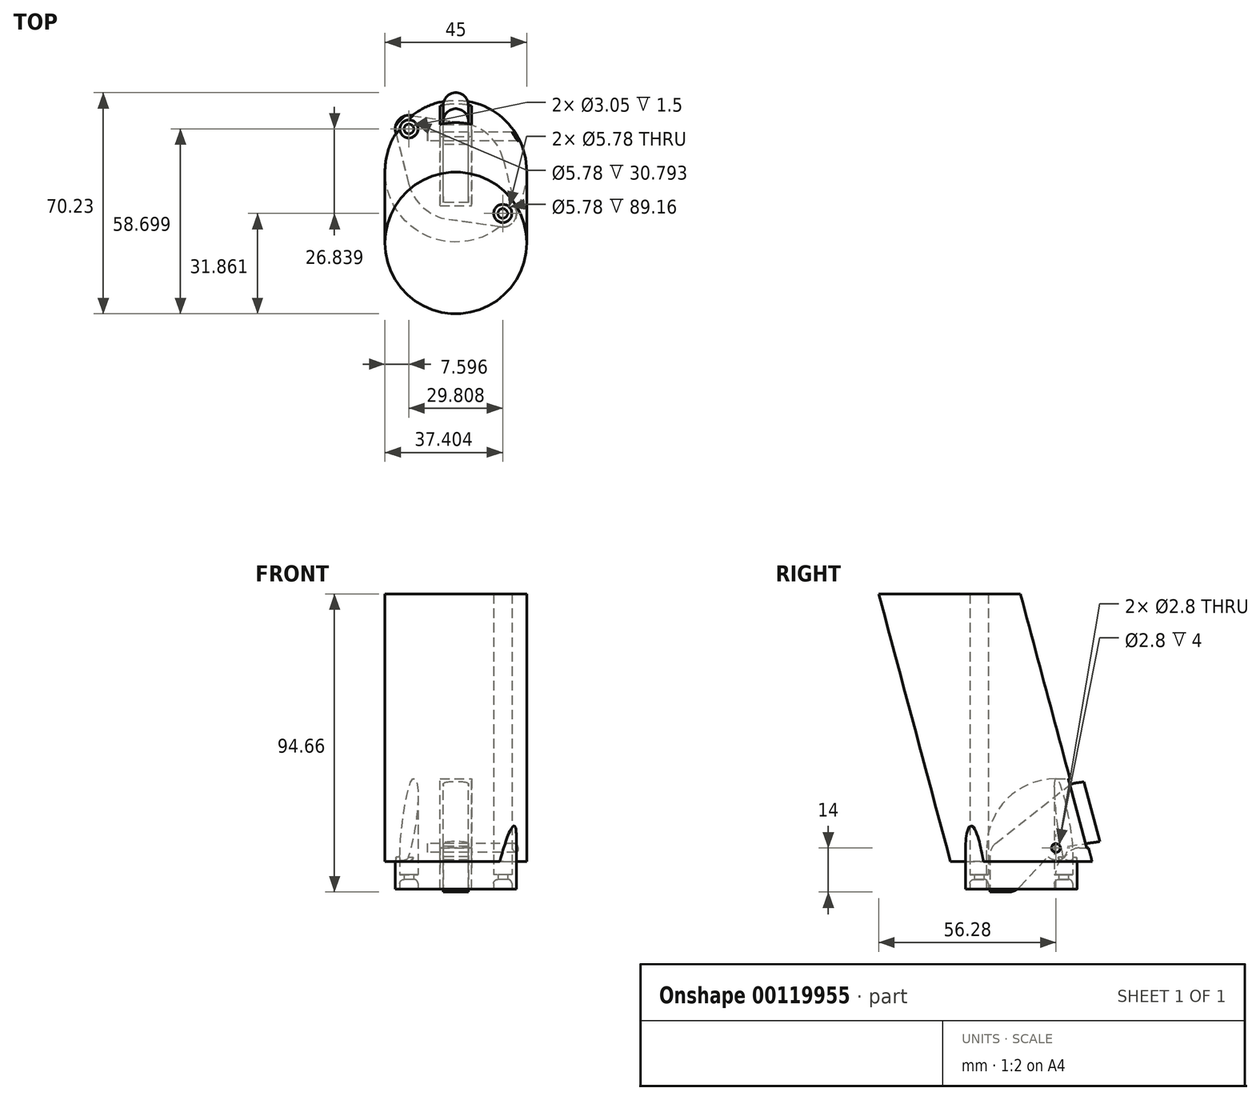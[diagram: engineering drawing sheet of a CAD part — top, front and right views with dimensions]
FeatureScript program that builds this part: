
annotation { "Feature Type Name" : "Feature", "Feature Type Description" : "" }
export const myFeature = defineFeature(function(context is Context, id is Id, definition is map)
    precondition{}
    {
        {
            var Q0;
            Q0=qCreatedBy(makeId("Top.planeOp"),FACE);
            var sketch = newSketch(context, id + "F0", { "sketchPlane" : qUnion([Q0])});
            skLineSegment(sketch, "E0", {"start": v(0, 52.12) * mm, "end": v(0, -55.22) * mm, "construction": true});
            skCircle(sketch, "E1", {"center": v(0, 0) * mm, "radius": 15.5 * mm});
            skCircle(sketch, "E2", {"center": v(-14.9, 13.42) * mm, "radius": 2.9 * mm});
            skCircle(sketch, "E3", {"center": v(-14.9, 13.42) * mm, "radius": 4.34 * mm});
            skCircle(sketch, "E4", {"center": v(-14.9, 13.42) * mm, "radius": 1.52 * mm});
            skCircle(sketch, "E5", {"center": v(14.9, -13.42) * mm, "radius": 1.52 * mm});
            skCircle(sketch, "E6", {"center": v(14.9, -13.42) * mm, "radius": 2.9 * mm});
            skCircle(sketch, "E7", {"center": v(14.9, -13.42) * mm, "radius": 4.34 * mm});
            skLineSegment(sketch, "E8", {"start": v(0, 0) * mm, "end": v(-14.9, 13.42) * mm, "construction": true});
            skLineSegment(sketch, "E9", {"start": v(0, 0) * mm, "end": v(14.9, -13.42) * mm, "construction": true});
            skLineSegment(sketch, "E10", {"start": v(-14.28, 17.72) * mm, "end": v(2.21, 15.34) * mm});
            skLineSegment(sketch, "E11", {"start": v(-19.12, 12.35) * mm, "end": v(-15.03, -3.8) * mm});
            skLineSegment(sketch, "E12", {"start": v(14.28, -17.72) * mm, "end": v(-2.21, -15.34) * mm});
            skLineSegment(sketch, "E13", {"start": v(15.03, 3.8) * mm, "end": v(19.12, -12.35) * mm});
            skSolve(sketch);
        }
        {
            var Q0;
            Q0=makeQuery(id+"F0.imprint","IMPRINT",FACE,{"disambiguationData":[TD([[makeQuery(id+"F0.imprint","IMPRINT",EDGE,{"derivedFrom":sQuery(id+"F0.wireOp",EDGE,"E2")}),-1.0]])]});
            var Q1;
            {var subQ0=sQuery(id+"F0.wireOp",EDGE,"E10");Q1=makeQuery(id+"F0.imprint","IMPRINT",FACE,{"disambiguationData":[TD([[makeQuery(id+"F0.imprint","IMPRINT",EDGE,{"derivedFrom":subQ0}),-1.0]])]});}
            var Q2;
            {var subQ0=sQuery(id+"F0.wireOp",EDGE,"E1");var subQ1=makeQuery(id+"F0.imprint","INTERSECT",VERTEX,{"derivedFrom":[subQ0,sQuery(id+"F0.wireOp",EDGE,"E10")]});Q2=makeQuery(id+"F0.imprint","IMPRINT",FACE,{"disambiguationData":[TD([[makeQuery(id+"F0.imprint","IMPRINT",EDGE,{"disambiguationData":[TD([[subQ1,1.0]])],"derivedFrom":subQ0}),1.0]])]});}
            var Q3;
            {var subQ0=sQuery(id+"F0.wireOp",EDGE,"E12");Q3=makeQuery(id+"F0.imprint","IMPRINT",FACE,{"disambiguationData":[TD([[makeQuery(id+"F0.imprint","IMPRINT",EDGE,{"derivedFrom":subQ0}),-1.0]])]});}
            var Q4;
            Q4=makeQuery(id+"F0.imprint","IMPRINT",FACE,{"disambiguationData":[TD([[makeQuery(id+"F0.imprint","IMPRINT",EDGE,{"derivedFrom":sQuery(id+"F0.wireOp",EDGE,"E6")}),-1.0]])]});
            extrude(context, id + "F1", {"entities" : qUnion([Q0, Q1, Q2, Q3, Q4]), "depth" : 8.66 * mm});
        }
        {
            var Q0;
            Q0=makeQuery(id+"F0.imprint","IMPRINT",FACE,{"disambiguationData":[TD([[makeQuery(id+"F0.imprint","IMPRINT",EDGE,{"derivedFrom":sQuery(id+"F0.wireOp",EDGE,"E5")}),-1.0]])]});
            var Q1;
            Q1=makeQuery(id+"F0.imprint","IMPRINT",FACE,{"disambiguationData":[TD([[makeQuery(id+"F0.imprint","IMPRINT",EDGE,{"derivedFrom":sQuery(id+"F0.wireOp",EDGE,"E2")}),1.0]])]});
            extrude(context, id + "F2", {"entities" : qUnion([Q0, Q1]), "operationType" : NewBodyOperationType.ADD, "depth" : 4.5 * mm});
        }
        {
            var Q0;
            Q0=makeQuery(id+"F0.imprint","IMPRINT",FACE,{"disambiguationData":[TD([[makeQuery(id+"F0.imprint","IMPRINT",EDGE,{"derivedFrom":sQuery(id+"F0.wireOp",EDGE,"E5")}),-1.0]])]});
            var Q1;
            Q1=makeQuery(id+"F0.imprint","IMPRINT",FACE,{"disambiguationData":[TD([[makeQuery(id+"F0.imprint","IMPRINT",EDGE,{"derivedFrom":sQuery(id+"F0.wireOp",EDGE,"E2")}),1.0]])]});
            extrude(context, id + "F3", {"entities" : qUnion([Q0, Q1]), "operationType" : NewBodyOperationType.REMOVE, "depth" : 3 * mm});
        }
        {
            var Q0;
            Q0=makeQuery(id+"F3.boolean.opBoolean","COPY",EDGE,{"derivedFrom":makeQuery(id+"F3.opExtrude","CAP_EDGE",EDGE,{"disambiguationData":[OSD([sQuery(id+"F0.wireOp",EDGE,"E6")])],"isStart":false})});
            var Q1;
            Q1=makeQuery(id+"F3.boolean.opBoolean","COPY",EDGE,{"derivedFrom":makeQuery(id+"F3.opExtrude","CAP_EDGE",EDGE,{"disambiguationData":[OSD([sQuery(id+"F0.wireOp",EDGE,"E2")])],"isStart":false})});
            fillet(context, id + "F4", {"entities" : qUnion([Q0, Q1]), "radius" : 1.3 * mm, "tangentPropagation" : true, "allowEdgeOverflow" : false});
        }
        {
            var Q0;
            Q0=makeQuery(id+"F1.opExtrude","CAP_FACE",FACE,{"disambiguationData":[OSD([sQuery(id+"F0.wireOp",EDGE,"E1"),sQuery(id+"F0.wireOp",EDGE,"E2"),sQuery(id+"F0.wireOp",EDGE,"E3"),sQuery(id+"F0.wireOp",EDGE,"E6"),sQuery(id+"F0.wireOp",EDGE,"E7"),sQuery(id+"F0.wireOp",EDGE,"E10"),sQuery(id+"F0.wireOp",EDGE,"E11"),sQuery(id+"F0.wireOp",EDGE,"E12"),sQuery(id+"F0.wireOp",EDGE,"E13")])],"isStart":false});
            var sketch = newSketch(context, id + "F5", { "sketchPlane" : qUnion([Q0])});
            skCircle(sketch, "E14", {"center": v(0, 0) * mm, "radius": 22.5 * mm});
            skSolve(sketch);
        }
        {
            var Q0;
            Q0=qCreatedBy(makeId("Right.planeOp"),FACE);
            var sketch = newSketch(context, id + "F6", { "sketchPlane" : qUnion([Q0])});
            skLineSegment(sketch, "E15", {"start": v(0, 8.66) * mm, "end": v(-22.78, 93.66) * mm});
            skLineSegment(sketch, "E16.0", {"start": v(3.8, 8.66) * mm, "end": v(-12.35, 8.66) * mm});
            skSolve(sketch);
        }
        {
            var Q0;
            {var subQ3=sQuery(id+"F0.wireOp",EDGE,"E1");var subQ14=sQuery(id+"F0.wireOp",EDGE,"E10");var subQ15=makeQuery(id+"F1.opExtrude","CAP_EDGE",EDGE,{"disambiguationData":[OSD([subQ3]),TDD([makeQuery(id+"F0.imprint","IMPRINT",EDGE,{"disambiguationData":[TD([[makeQuery(id+"F0.imprint","INTERSECT",VERTEX,{"derivedFrom":[subQ3,subQ14]}),1.0]])],"derivedFrom":subQ3})])],"isStart":false});Q0=makeQuery(id+"F5.imprint","IMPRINT",FACE,{"disambiguationData":[TD([[makeQuery(id+"F5.imprint","IMPRINT",EDGE,{"derivedFrom":subQ15}),1.0]])]});}
            var Q1;
            {var subQ0=sQuery(id+"F5.wireOp",EDGE,"E14");var subQ1=makeQuery(id+"F1.opExtrude","CAP_EDGE",EDGE,{"disambiguationData":[OSD([sQuery(id+"F0.wireOp",EDGE,"E6")])],"isStart":false});var subQ2=makeQuery(id+"F5.imprint","INTERSECT",VERTEX,{"disambiguationData":[OD(0.0)],"derivedFrom":[subQ1,subQ0]});Q1=makeQuery(id+"F5.imprint","IMPRINT",FACE,{"disambiguationData":[TD([[makeQuery(id+"F5.imprint","IMPRINT",EDGE,{"disambiguationData":[TD([[subQ2,-1.0]])],"derivedFrom":subQ0}),1.0]])]});}
            var Q2;
            {var subQ0=sQuery(id+"F5.wireOp",EDGE,"E14");var subQ1=makeQuery(id+"F1.opExtrude","CAP_EDGE",EDGE,{"disambiguationData":[OSD([sQuery(id+"F0.wireOp",EDGE,"E2")])],"isStart":false});var subQ2=makeQuery(id+"F5.imprint","INTERSECT",VERTEX,{"disambiguationData":[OD(0.0)],"derivedFrom":[subQ1,subQ0]});Q2=makeQuery(id+"F5.imprint","IMPRINT",FACE,{"disambiguationData":[TD([[makeQuery(id+"F5.imprint","IMPRINT",EDGE,{"disambiguationData":[TD([[subQ2,-1.0]])],"derivedFrom":subQ0}),1.0]])]});}
            var Q3;
            {var subQ1=sQuery(id+"F0.wireOp",EDGE,"E10");var subQ7=sQuery(id+"F0.wireOp",EDGE,"E1");var subQ8=makeQuery(id+"F1.opExtrude","CAP_EDGE",EDGE,{"disambiguationData":[OSD([subQ7]),TDD([makeQuery(id+"F0.imprint","IMPRINT",EDGE,{"disambiguationData":[TD([[makeQuery(id+"F0.imprint","INTERSECT",VERTEX,{"derivedFrom":[subQ7,subQ1]}),1.0]])],"derivedFrom":subQ7})])],"isStart":false});Q3=makeQuery(id+"F5.imprint","IMPRINT",FACE,{"disambiguationData":[TD([[makeQuery(id+"F5.imprint","IMPRINT",EDGE,{"derivedFrom":subQ8}),-1.0]])]});}
            var Q4;
            {var subQ1=sQuery(id+"F0.wireOp",EDGE,"E11");var subQ7=sQuery(id+"F0.wireOp",EDGE,"E1");var subQ8=makeQuery(id+"F1.opExtrude","CAP_EDGE",EDGE,{"disambiguationData":[OSD([subQ7]),TDD([makeQuery(id+"F0.imprint","IMPRINT",EDGE,{"disambiguationData":[TD([[makeQuery(id+"F0.imprint","INTERSECT",VERTEX,{"derivedFrom":[subQ7,subQ1]}),-1.0]])],"derivedFrom":subQ7})])],"isStart":false});Q4=makeQuery(id+"F5.imprint","IMPRINT",FACE,{"disambiguationData":[TD([[makeQuery(id+"F5.imprint","IMPRINT",EDGE,{"derivedFrom":subQ8}),-1.0]])]});}
            var Q5;
            Q5=sQuery(id+"F6.wireOp",EDGE,"E15");
            sweep(context, id + "F7", {"operationType" : NewBodyOperationType.ADD, "profiles" : qUnion([Q0, Q1, Q2, Q3, Q4]), "path" : qUnion([Q5])});
        }
        {
            var Q0;
            {var subQ0=sQuery(id+"F0.wireOp",EDGE,"E13");var subQ1=sQuery(id+"F0.wireOp",EDGE,"E12");var subQ2=sQuery(id+"F0.wireOp",EDGE,"E7");var subQ4=sQuery(id+"F0.wireOp",EDGE,"E6");Q0=makeQuery(id+"F7.boolean.opBoolean","SPLIT",FACE,{"disambiguationData":[TD([makeQuery(id+"F1.opExtrude","SWEPT_FACE",FACE,{"disambiguationData":[OSD([subQ4])]})])],"derivedFrom":makeQuery(id+"F1.opExtrude","CAP_FACE",FACE,{"disambiguationData":[OSD([sQuery(id+"F0.wireOp",EDGE,"E1"),sQuery(id+"F0.wireOp",EDGE,"E2"),sQuery(id+"F0.wireOp",EDGE,"E3"),subQ4,subQ2,sQuery(id+"F0.wireOp",EDGE,"E10"),sQuery(id+"F0.wireOp",EDGE,"E11"),subQ1,subQ0])],"isStart":false})});}
            var sketch = newSketch(context, id + "F8", { "sketchPlane" : qUnion([Q0])});
            skArc(sketch, "E17.0", {"start": v(15.59, -16.23) * mm, "mid": v(17.05, -15.35) * mm, "end": v(17.77, -13.8) * mm});
            skArc(sketch, "E18.0", {"start": v(17.77, -13.8) * mm, "mid": v(12.76, -11.49) * mm, "end": v(15.59, -16.23) * mm});
            skSolve(sketch);
        }
        {
            var Q0;
            {var subQ0=sQuery(id+"F0.wireOp",EDGE,"E6");var subQ1=sQuery(id+"F5.wireOp",EDGE,"E14");Q0=makeQuery(id+"F7.boolean.opBoolean","SPLIT",FACE,{"disambiguationData":[TD([makeQuery(id+"F1.opExtrude","SWEPT_FACE",FACE,{"disambiguationData":[OSD([subQ0])]})])],"derivedFrom":makeQuery(id+"F7.opSweep","CAP_FACE",FACE,{"disambiguationData":[OSD([subQ1,sQuery(id+"F6.wireOp",VERTEX,"E15.start")])],"isStart":true})});}
            var Q1;
            {var subQ0=sQuery(id+"F0.wireOp",EDGE,"E2");var subQ1=sQuery(id+"F5.wireOp",EDGE,"E14");Q1=makeQuery(id+"F7.boolean.opBoolean","SPLIT",FACE,{"disambiguationData":[TD([makeQuery(id+"F1.opExtrude","SWEPT_FACE",FACE,{"disambiguationData":[OSD([subQ0])]})])],"derivedFrom":makeQuery(id+"F7.opSweep","CAP_FACE",FACE,{"disambiguationData":[OSD([subQ1,sQuery(id+"F6.wireOp",VERTEX,"E15.start")])],"isStart":true})});}
            var Q2;
            Q2=makeQuery(id+"F8.imprint","IMPRINT",FACE,{"disambiguationData":[TD([[makeQuery(id+"F8.imprint","IMPRINT",EDGE,{"derivedFrom":sQuery(id+"F8.wireOp",EDGE,"E17.0")}),1.0]])]});
            extrude(context, id + "F9", {"entities" : qUnion([Q0, Q1, Q2]), "operationType" : NewBodyOperationType.REMOVE, "endBound" : BoundingType.THROUGH_ALL, "oppositeDirection" : true, "depth" : 25 * mm});
        }
        {
            var Q0;
            {var subQ0=sQuery(id+"F6.wireOp",VERTEX,"E15.start");var subQ1=sQuery(id+"F5.wireOp",EDGE,"E14");var subQ2=sQuery(id+"F0.wireOp",EDGE,"E2");var subQ3=sQuery(id+"F0.wireOp",EDGE,"E10");Q0=makeQuery(id+"F7.boolean.opBoolean","SPLIT",EDGE,{"disambiguationData":[TD([makeQuery(id+"F1.opExtrude","CAP_FACE",FACE,{"disambiguationData":[OSD([sQuery(id+"F0.wireOp",EDGE,"E1"),subQ2,sQuery(id+"F0.wireOp",EDGE,"E3"),sQuery(id+"F0.wireOp",EDGE,"E6"),sQuery(id+"F0.wireOp",EDGE,"E7"),subQ3,sQuery(id+"F0.wireOp",EDGE,"E11"),sQuery(id+"F0.wireOp",EDGE,"E12"),sQuery(id+"F0.wireOp",EDGE,"E13")])],"isStart":false}),makeQuery(id+"F1.opExtrude","SWEPT_FACE",FACE,{"disambiguationData":[OSD([subQ2])]}),makeQuery(id+"F1.opExtrude","SWEPT_FACE",FACE,{"disambiguationData":[OSD([subQ3])]}),makeQuery(id+"F7.opSweep","CAP_FACE",FACE,{"disambiguationData":[OSD([subQ1,subQ0])],"isStart":true}),makeQuery(id+"F7.opSweep","SWEPT_FACE",FACE,{"disambiguationData":[OSD([subQ1,sQuery(id+"F6.wireOp",EDGE,"E15")])]})])],"derivedFrom":makeQuery(id+"F7.opSweep","CAP_EDGE",EDGE,{"disambiguationData":[OSD([subQ1,subQ0])],"isStart":true})});}
            var Q1;
            {var subQ0=sQuery(id+"F6.wireOp",VERTEX,"E15.start");var subQ1=sQuery(id+"F5.wireOp",EDGE,"E14");var subQ2=sQuery(id+"F0.wireOp",EDGE,"E11");var subQ3=sQuery(id+"F0.wireOp",EDGE,"E2");Q1=makeQuery(id+"F7.boolean.opBoolean","SPLIT",EDGE,{"disambiguationData":[TD([makeQuery(id+"F1.opExtrude","CAP_FACE",FACE,{"disambiguationData":[OSD([sQuery(id+"F0.wireOp",EDGE,"E1"),subQ3,sQuery(id+"F0.wireOp",EDGE,"E3"),sQuery(id+"F0.wireOp",EDGE,"E6"),sQuery(id+"F0.wireOp",EDGE,"E7"),sQuery(id+"F0.wireOp",EDGE,"E10"),subQ2,sQuery(id+"F0.wireOp",EDGE,"E12"),sQuery(id+"F0.wireOp",EDGE,"E13")])],"isStart":false}),makeQuery(id+"F1.opExtrude","SWEPT_FACE",FACE,{"disambiguationData":[OSD([subQ3])]}),makeQuery(id+"F1.opExtrude","SWEPT_FACE",FACE,{"disambiguationData":[OSD([subQ2])]}),makeQuery(id+"F7.opSweep","CAP_FACE",FACE,{"disambiguationData":[OSD([subQ1,subQ0])],"isStart":true}),makeQuery(id+"F7.opSweep","SWEPT_FACE",FACE,{"disambiguationData":[OSD([subQ1,sQuery(id+"F6.wireOp",EDGE,"E15")])]})])],"derivedFrom":makeQuery(id+"F7.opSweep","CAP_EDGE",EDGE,{"disambiguationData":[OSD([subQ1,subQ0])],"isStart":true})});}
            fillet(context, id + "F10", {"entities" : qUnion([Q0, Q1]), "radius" : 1.7 * mm, "tangentPropagation" : true, "allowEdgeOverflow" : false});
        }
        {
            var Q0;
            {var subQ0=sQuery(id+"F0.wireOp",EDGE,"E13");var subQ1=sQuery(id+"F0.wireOp",EDGE,"E12");var subQ2=sQuery(id+"F0.wireOp",EDGE,"E7");var subQ4=sQuery(id+"F0.wireOp",EDGE,"E6");Q0=makeQuery(id+"F7.boolean.opBoolean","SPLIT",FACE,{"disambiguationData":[TD([makeQuery(id+"F1.opExtrude","SWEPT_FACE",FACE,{"disambiguationData":[OSD([subQ4])]})])],"derivedFrom":makeQuery(id+"F1.opExtrude","CAP_FACE",FACE,{"disambiguationData":[OSD([sQuery(id+"F0.wireOp",EDGE,"E1"),sQuery(id+"F0.wireOp",EDGE,"E2"),sQuery(id+"F0.wireOp",EDGE,"E3"),subQ4,subQ2,sQuery(id+"F0.wireOp",EDGE,"E10"),sQuery(id+"F0.wireOp",EDGE,"E11"),subQ1,subQ0])],"isStart":false})});}
            var Q1;
            Q1=makeQuery(id+"F1.opExtrude","SWEPT_BODY",BODY,{"disambiguationData":[OSD([sQuery(id+"F0.wireOp",EDGE,"E1"),sQuery(id+"F0.wireOp",EDGE,"E2"),sQuery(id+"F0.wireOp",EDGE,"E3"),sQuery(id+"F0.wireOp",EDGE,"E6"),sQuery(id+"F0.wireOp",EDGE,"E7"),sQuery(id+"F0.wireOp",EDGE,"E10"),sQuery(id+"F0.wireOp",EDGE,"E11"),sQuery(id+"F0.wireOp",EDGE,"E12"),sQuery(id+"F0.wireOp",EDGE,"E13")])]});
            extrude(context, id + "F11", {"entities" : qUnion([Q0]), "operationType" : NewBodyOperationType.ADD, "endBound" : BoundingType.UP_TO_BODY, "endBoundEntityBody" : qUnion([Q1]), "depth" : 25 * mm});
        }
        {
            var Q0;
            Q0=qCreatedBy(makeId("Right.planeOp"),FACE);
            var sketch = newSketch(context, id + "F12", { "sketchPlane" : qUnion([Q0])});
            skLineSegment(sketch, "E19", {"start": v(-11, 0) * mm, "end": v(11, 0) * mm});
            skLineSegment(sketch, "E20", {"start": v(-11, 0) * mm, "end": v(-11, 13) * mm});
            skLineSegment(sketch, "E21", {"start": v(11, 0) * mm, "end": v(11, 13) * mm});
            skArc(sketch, "E22", {"start": v(-11, 13) * mm, "mid": v(-4.56, 28.56) * mm, "end": v(11, 35) * mm});
            skLineSegment(sketch, "E23", {"start": v(11, 35) * mm, "end": v(17.1, 35) * mm});
            skLineSegment(sketch, "E24", {"start": v(11, 13) * mm, "end": v(23, 13) * mm});
            skLineSegment(sketch, "E25", {"start": v(23, 13) * mm, "end": v(17.1, 35) * mm});
            skCircle(sketch, "E26", {"center": v(11, 13) * mm, "radius": 1.4 * mm});
            skCircle(sketch, "E27", {"center": v(11, 13) * mm, "radius": 4 * mm});
            skCircle(sketch, "E28", {"center": v(11, 13) * mm, "radius": 3.75 * mm});
            skLineSegment(sketch, "E29", {"start": v(-10, 13) * mm, "end": v(-10, -1) * mm});
            skLineSegment(sketch, "E30", {"start": v(-10, -1) * mm, "end": v(-2, -1) * mm});
            skLineSegment(sketch, "E31", {"start": v(-2, -1) * mm, "end": v(11, 13) * mm});
            skLineSegment(sketch, "E32", {"start": v(11, 13) * mm, "end": v(24.95, 15.03) * mm});
            skLineSegment(sketch, "E33", {"start": v(24.95, 15.03) * mm, "end": v(19.86, 34.02) * mm});
            skLineSegment(sketch, "E34", {"start": v(15.9, 33.44) * mm, "end": v(19.86, 34.02) * mm});
            skLineSegment(sketch, "E35", {"start": v(-10, 13) * mm, "end": v(15.9, 33.44) * mm});
            skSolve(sketch);
        }
        {
            var Q0;
            {var subQ1=sQuery(id+"F12.wireOp",EDGE,"E20");Q0=makeQuery(id+"F12.imprint","IMPRINT",FACE,{"disambiguationData":[TD([[makeQuery(id+"F12.imprint","IMPRINT",EDGE,{"derivedFrom":subQ1}),-1.0]])]});}
            var Q1;
            {var subQ5=sQuery(id+"F12.wireOp",EDGE,"xrNV4oZF-NdtU-CIpK-rpjW-CCXHllgnYPWw");Q1=makeQuery(id+"F12.imprint","IMPRINT",FACE,{"disambiguationData":[TD([[makeQuery(id+"F12.imprint","IMPRINT",EDGE,{"derivedFrom":subQ5}),-1.0]])]});}
            var Q2;
            {var subQ0=sQuery(id+"F12.wireOp",EDGE,"E21");var subQ1=sQuery(id+"F12.wireOp",EDGE,"E19");var subQ2=makeQuery(id+"F12.imprint","INTERSECT",VERTEX,{"derivedFrom":[subQ1,subQ0]});Q2=makeQuery(id+"F12.imprint","IMPRINT",FACE,{"disambiguationData":[TD([[makeQuery(id+"F12.imprint","IMPRINT",EDGE,{"disambiguationData":[TD([[subQ2,1.0]])],"derivedFrom":subQ1}),1.0]])]});}
            var Q3;
            {var subQ0=sQuery(id+"F12.wireOp",EDGE,"E32");var subQ1=sQuery(id+"F12.wireOp",EDGE,"E27");var subQ2=makeQuery(id+"F12.imprint","INTERSECT",VERTEX,{"derivedFrom":[subQ1,subQ0]});Q3=makeQuery(id+"F12.imprint","IMPRINT",FACE,{"disambiguationData":[TD([[makeQuery(id+"F12.imprint","IMPRINT",EDGE,{"disambiguationData":[TD([[subQ2,-1.0]])],"derivedFrom":subQ1}),1.0]])]});}
            var Q4;
            {var subQ0=sQuery(id+"F12.wireOp",EDGE,"E32");var subQ1=sQuery(id+"F12.wireOp",EDGE,"E26");var subQ2=makeQuery(id+"F12.imprint","INTERSECT",VERTEX,{"derivedFrom":[subQ1,subQ0]});Q4=makeQuery(id+"F12.imprint","IMPRINT",FACE,{"disambiguationData":[TD([[makeQuery(id+"F12.imprint","IMPRINT",EDGE,{"disambiguationData":[TD([[subQ2,-1.0]])],"derivedFrom":subQ1}),-1.0]])]});}
            var Q5;
            {var subQ0=sQuery(id+"F12.wireOp",EDGE,"E32");var subQ1=sQuery(id+"F12.wireOp",EDGE,"E26");var subQ2=makeQuery(id+"F12.imprint","INTERSECT",VERTEX,{"derivedFrom":[subQ1,subQ0]});Q5=makeQuery(id+"F12.imprint","IMPRINT",FACE,{"disambiguationData":[TD([[makeQuery(id+"F12.imprint","IMPRINT",EDGE,{"disambiguationData":[TD([[subQ2,-1.0]])],"derivedFrom":subQ1}),1.0]])]});}
            var Q6;
            {var subQ1=sQuery(id+"F12.wireOp",EDGE,"E21");var subQ3=sQuery(id+"F12.wireOp",EDGE,"E26");var subQ4=makeQuery(id+"F12.imprint","INTERSECT",VERTEX,{"derivedFrom":[subQ1,subQ3]});Q6=makeQuery(id+"F12.imprint","IMPRINT",FACE,{"disambiguationData":[TD([[makeQuery(id+"F12.imprint","IMPRINT",EDGE,{"disambiguationData":[TD([[subQ4,1.0]])],"derivedFrom":subQ3}),1.0]])]});}
            var Q7;
            {var subQ1=sQuery(id+"F12.wireOp",EDGE,"E21");var subQ3=sQuery(id+"F12.wireOp",EDGE,"E26");var subQ4=makeQuery(id+"F12.imprint","INTERSECT",VERTEX,{"derivedFrom":[subQ1,subQ3]});Q7=makeQuery(id+"F12.imprint","IMPRINT",FACE,{"disambiguationData":[TD([[makeQuery(id+"F12.imprint","IMPRINT",EDGE,{"disambiguationData":[TD([[subQ4,-1.0]])],"derivedFrom":subQ3}),1.0]])]});}
            var Q8;
            {var subQ1=sQuery(id+"F12.wireOp",EDGE,"E24");var subQ3=sQuery(id+"F12.wireOp",EDGE,"E26");var subQ4=makeQuery(id+"F12.imprint","INTERSECT",VERTEX,{"derivedFrom":[subQ1,subQ3]});Q8=makeQuery(id+"F12.imprint","IMPRINT",FACE,{"disambiguationData":[TD([[makeQuery(id+"F12.imprint","IMPRINT",EDGE,{"disambiguationData":[TD([[subQ4,-1.0]])],"derivedFrom":subQ3}),1.0]])]});}
            var Q9;
            {var subQ0=sQuery(id+"F12.wireOp",EDGE,"E28");var subQ1=sQuery(id+"F12.wireOp",EDGE,"E21");var subQ2=makeQuery(id+"F12.imprint","INTERSECT",VERTEX,{"derivedFrom":[subQ1,subQ0]});Q9=makeQuery(id+"F12.imprint","IMPRINT",FACE,{"disambiguationData":[TD([[makeQuery(id+"F12.imprint","IMPRINT",EDGE,{"disambiguationData":[TD([[subQ2,-1.0]])],"derivedFrom":subQ1}),-1.0]])]});}
            var Q10;
            {var subQ0=sQuery(id+"F12.wireOp",EDGE,"E28");var subQ1=sQuery(id+"F12.wireOp",EDGE,"E21");var subQ2=makeQuery(id+"F12.imprint","INTERSECT",VERTEX,{"derivedFrom":[subQ1,subQ0]});Q10=makeQuery(id+"F12.imprint","IMPRINT",FACE,{"disambiguationData":[TD([[makeQuery(id+"F12.imprint","IMPRINT",EDGE,{"disambiguationData":[TD([[subQ2,-1.0]])],"derivedFrom":subQ1}),1.0]])]});}
            var Q11;
            {var subQ0=sQuery(id+"F12.wireOp",EDGE,"E26");var subQ1=sQuery(id+"F12.wireOp",EDGE,"E24");var subQ2=makeQuery(id+"F12.imprint","INTERSECT",VERTEX,{"derivedFrom":[subQ1,subQ0]});Q11=makeQuery(id+"F12.imprint","IMPRINT",FACE,{"disambiguationData":[TD([[makeQuery(id+"F12.imprint","IMPRINT",EDGE,{"disambiguationData":[TD([[subQ2,-1.0]])],"derivedFrom":subQ1}),1.0]])]});}
            var Q12;
            {var subQ0=sQuery(id+"F12.wireOp",EDGE,"E27");var subQ1=sQuery(id+"F12.wireOp",EDGE,"E24");var subQ2=makeQuery(id+"F12.imprint","INTERSECT",VERTEX,{"derivedFrom":[subQ1,subQ0]});Q12=makeQuery(id+"F12.imprint","IMPRINT",FACE,{"disambiguationData":[TD([[makeQuery(id+"F12.imprint","IMPRINT",EDGE,{"disambiguationData":[TD([[subQ2,1.0]])],"derivedFrom":subQ1}),1.0]])]});}
            var Q13;
            {var subQ0=sQuery(id+"F12.wireOp",EDGE,"E27");var subQ1=sQuery(id+"F12.wireOp",EDGE,"E21");var subQ2=makeQuery(id+"F12.imprint","INTERSECT",VERTEX,{"derivedFrom":[subQ1,subQ0]});Q13=makeQuery(id+"F12.imprint","IMPRINT",FACE,{"disambiguationData":[TD([[makeQuery(id+"F12.imprint","IMPRINT",EDGE,{"disambiguationData":[TD([[subQ2,-1.0]])],"derivedFrom":subQ1}),-1.0]])]});}
            var Q14;
            {var subQ0=sQuery(id+"F12.wireOp",EDGE,"E27");var subQ1=sQuery(id+"F12.wireOp",EDGE,"E21");var subQ2=makeQuery(id+"F12.imprint","INTERSECT",VERTEX,{"derivedFrom":[subQ1,subQ0]});Q14=makeQuery(id+"F12.imprint","IMPRINT",FACE,{"disambiguationData":[TD([[makeQuery(id+"F12.imprint","IMPRINT",EDGE,{"disambiguationData":[TD([[subQ2,-1.0]])],"derivedFrom":subQ1}),1.0]])]});}
            var Q15;
            {var subQ0=sQuery(id+"F12.wireOp",EDGE,"E25");var subQ1=sQuery(id+"F12.wireOp",EDGE,"E24");var subQ2=makeQuery(id+"F12.imprint","INTERSECT",VERTEX,{"derivedFrom":[subQ1,subQ0]});Q15=makeQuery(id+"F12.imprint","IMPRINT",FACE,{"disambiguationData":[TD([[makeQuery(id+"F12.imprint","IMPRINT",EDGE,{"disambiguationData":[TD([[subQ2,1.0]])],"derivedFrom":subQ1}),1.0]])]});}
            var Q16;
            {var subQ5=sQuery(id+"F12.wireOp",EDGE,"E35");Q16=makeQuery(id+"F12.imprint","IMPRINT",FACE,{"disambiguationData":[TD([[makeQuery(id+"F12.imprint","IMPRINT",EDGE,{"derivedFrom":subQ5}),-1.0]])]});}
            extrude(context, id + "F13", {"entities" : qUnion([Q0, Q1, Q2, Q3, Q4, Q5, Q6, Q7, Q8, Q9, Q10, Q11, Q12, Q13, Q14, Q15, Q16]), "operationType" : NewBodyOperationType.REMOVE, "endBound" : BoundingType.SYMMETRIC, "oppositeDirection" : true, "depth" : 10 * mm});
        }
        {
            var Q0;
            {var subQ1=sQuery(id+"F12.wireOp",EDGE,"E24");var subQ3=sQuery(id+"F12.wireOp",EDGE,"E26");var subQ4=makeQuery(id+"F12.imprint","INTERSECT",VERTEX,{"derivedFrom":[subQ1,subQ3]});Q0=makeQuery(id+"F12.imprint","IMPRINT",FACE,{"disambiguationData":[TD([[makeQuery(id+"F12.imprint","IMPRINT",EDGE,{"disambiguationData":[TD([[subQ4,-1.0]])],"derivedFrom":subQ3}),1.0]])]});}
            var Q1;
            {var subQ1=sQuery(id+"F12.wireOp",EDGE,"E21");var subQ3=sQuery(id+"F12.wireOp",EDGE,"E26");var subQ4=makeQuery(id+"F12.imprint","INTERSECT",VERTEX,{"derivedFrom":[subQ1,subQ3]});Q1=makeQuery(id+"F12.imprint","IMPRINT",FACE,{"disambiguationData":[TD([[makeQuery(id+"F12.imprint","IMPRINT",EDGE,{"disambiguationData":[TD([[subQ4,-1.0]])],"derivedFrom":subQ3}),1.0]])]});}
            var Q2;
            {var subQ1=sQuery(id+"F12.wireOp",EDGE,"E21");var subQ3=sQuery(id+"F12.wireOp",EDGE,"E26");var subQ4=makeQuery(id+"F12.imprint","INTERSECT",VERTEX,{"derivedFrom":[subQ1,subQ3]});Q2=makeQuery(id+"F12.imprint","IMPRINT",FACE,{"disambiguationData":[TD([[makeQuery(id+"F12.imprint","IMPRINT",EDGE,{"disambiguationData":[TD([[subQ4,1.0]])],"derivedFrom":subQ3}),1.0]])]});}
            var Q3;
            {var subQ0=sQuery(id+"F12.wireOp",EDGE,"E32");var subQ1=sQuery(id+"F12.wireOp",EDGE,"E26");var subQ2=makeQuery(id+"F12.imprint","INTERSECT",VERTEX,{"derivedFrom":[subQ1,subQ0]});Q3=makeQuery(id+"F12.imprint","IMPRINT",FACE,{"disambiguationData":[TD([[makeQuery(id+"F12.imprint","IMPRINT",EDGE,{"disambiguationData":[TD([[subQ2,-1.0]])],"derivedFrom":subQ1}),1.0]])]});}
            extrude(context, id + "F14", {"entities" : qUnion([Q0, Q1, Q2, Q3]), "operationType" : NewBodyOperationType.REMOVE, "endBound" : BoundingType.THROUGH_ALL, "depth" : 45 * mm, "hasSecondDirection" : true, "secondDirectionOppositeDirection" : true, "secondDirectionDepth" : 9 * mm});
        }
        {
            var Q0;
            Q0=makeQuery(id+"F13.boolean.opBoolean","COPY",EDGE,{"derivedFrom":makeQuery(id+"F13.opExtrude","SWEPT_EDGE",EDGE,{"disambiguationData":[OSD([sQuery(id+"F12.wireOp",EDGE,"E27"),sQuery(id+"F12.wireOp",EDGE,"E32")])]})});
            var Q1;
            Q1=makeQuery(id+"F13.boolean.opBoolean","COPY",EDGE,{"derivedFrom":makeQuery(id+"F13.opExtrude","SWEPT_EDGE",EDGE,{"disambiguationData":[OSD([sQuery(id+"F12.wireOp",EDGE,"E21"),sQuery(id+"F12.wireOp",EDGE,"E27")])]})});
            fillet(context, id + "F15", {"entities" : qUnion([Q0, Q1]), "radius" : 5 * mm, "tangentPropagation" : true, "allowEdgeOverflow" : false});
        }
        {
            var Q0;
            {var subQ5=sQuery(id+"F12.wireOp",EDGE,"xrNV4oZF-NdtU-CIpK-rpjW-CCXHllgnYPWw");Q0=makeQuery(id+"F12.imprint","IMPRINT",FACE,{"disambiguationData":[TD([[makeQuery(id+"F12.imprint","IMPRINT",EDGE,{"derivedFrom":subQ5}),-1.0]])]});}
            var Q1;
            {var subQ5=sQuery(id+"F12.wireOp",EDGE,"E33");Q1=makeQuery(id+"F12.imprint","IMPRINT",FACE,{"disambiguationData":[TD([[makeQuery(id+"F12.imprint","IMPRINT",EDGE,{"derivedFrom":subQ5}),1.0]])]});}
            var Q2;
            {var subQ0=sQuery(id+"F12.wireOp",EDGE,"E32");var subQ1=sQuery(id+"F12.wireOp",EDGE,"E26");var subQ2=makeQuery(id+"F12.imprint","INTERSECT",VERTEX,{"derivedFrom":[subQ1,subQ0]});Q2=makeQuery(id+"F12.imprint","IMPRINT",FACE,{"disambiguationData":[TD([[makeQuery(id+"F12.imprint","IMPRINT",EDGE,{"disambiguationData":[TD([[subQ2,-1.0]])],"derivedFrom":subQ1}),-1.0]])]});}
            var Q3;
            {var subQ0=sQuery(id+"F12.wireOp",EDGE,"E32");var subQ1=sQuery(id+"F12.wireOp",EDGE,"E27");var subQ2=makeQuery(id+"F12.imprint","INTERSECT",VERTEX,{"derivedFrom":[subQ1,subQ0]});Q3=makeQuery(id+"F12.imprint","IMPRINT",FACE,{"disambiguationData":[TD([[makeQuery(id+"F12.imprint","IMPRINT",EDGE,{"disambiguationData":[TD([[subQ2,-1.0]])],"derivedFrom":subQ1}),1.0]])]});}
            var Q4;
            {var subQ0=sQuery(id+"F12.wireOp",EDGE,"E28");var subQ1=sQuery(id+"F12.wireOp",EDGE,"E21");var subQ2=makeQuery(id+"F12.imprint","INTERSECT",VERTEX,{"derivedFrom":[subQ1,subQ0]});Q4=makeQuery(id+"F12.imprint","IMPRINT",FACE,{"disambiguationData":[TD([[makeQuery(id+"F12.imprint","IMPRINT",EDGE,{"disambiguationData":[TD([[subQ2,-1.0]])],"derivedFrom":subQ1}),1.0]])]});}
            var Q5;
            {var subQ0=sQuery(id+"F12.wireOp",EDGE,"E28");var subQ1=sQuery(id+"F12.wireOp",EDGE,"E21");var subQ2=makeQuery(id+"F12.imprint","INTERSECT",VERTEX,{"derivedFrom":[subQ1,subQ0]});Q5=makeQuery(id+"F12.imprint","IMPRINT",FACE,{"disambiguationData":[TD([[makeQuery(id+"F12.imprint","IMPRINT",EDGE,{"disambiguationData":[TD([[subQ2,-1.0]])],"derivedFrom":subQ1}),-1.0]])]});}
            var Q6;
            {var subQ0=sQuery(id+"F12.wireOp",EDGE,"E26");var subQ1=sQuery(id+"F12.wireOp",EDGE,"E24");var subQ2=makeQuery(id+"F12.imprint","INTERSECT",VERTEX,{"derivedFrom":[subQ1,subQ0]});Q6=makeQuery(id+"F12.imprint","IMPRINT",FACE,{"disambiguationData":[TD([[makeQuery(id+"F12.imprint","IMPRINT",EDGE,{"disambiguationData":[TD([[subQ2,-1.0]])],"derivedFrom":subQ1}),1.0]])]});}
            var Q7;
            {var subQ5=sQuery(id+"F12.wireOp",EDGE,"E30");Q7=makeQuery(id+"F12.imprint","IMPRINT",FACE,{"disambiguationData":[TD([[makeQuery(id+"F12.imprint","IMPRINT",EDGE,{"derivedFrom":subQ5}),1.0]])]});}
            var Q8;
            {var subQ5=sQuery(id+"F12.wireOp",EDGE,"E35");Q8=makeQuery(id+"F12.imprint","IMPRINT",FACE,{"disambiguationData":[TD([[makeQuery(id+"F12.imprint","IMPRINT",EDGE,{"derivedFrom":subQ5}),-1.0]])]});}
            extrude(context, id + "F16", {"entities" : qUnion([Q0, Q1, Q2, Q3, Q4, Q5, Q6, Q7, Q8]), "endBound" : BoundingType.SYMMETRIC, "depth" : 8 * mm});
        }
        {
            var Q0;
            Q0=makeQuery(id+"F16.opExtrude","CAP_EDGE",EDGE,{"disambiguationData":[OSD([sQuery(id+"F12.wireOp",EDGE,"E33")])],"isStart":false});
            var Q1;
            Q1=makeQuery(id+"F16.opExtrude","CAP_EDGE",EDGE,{"disambiguationData":[OSD([sQuery(id+"F12.wireOp",EDGE,"E33")])],"isStart":true});
            fillet(context, id + "F17", {"entities" : qUnion([Q0, Q1]), "radius" : 4 * mm, "tangentPropagation" : true, "allowEdgeOverflow" : false});
        }
        {
            var Q0;
            Q0=makeQuery(id+"F16.opExtrude","SWEPT_EDGE",EDGE,{"disambiguationData":[OSD([sQuery(id+"F12.wireOp",EDGE,"E34"),sQuery(id+"F12.wireOp",EDGE,"E35")])]});
            var Q1;
            Q1=makeQuery(id+"F16.opExtrude","SWEPT_EDGE",EDGE,{"disambiguationData":[OSD([sQuery(id+"F12.wireOp",EDGE,"E29"),sQuery(id+"F12.wireOp",EDGE,"E35")])]});
            var Q2;
            Q2=makeQuery(id+"F16.opExtrude","SWEPT_EDGE",EDGE,{"disambiguationData":[OSD([sQuery(id+"F12.wireOp",EDGE,"E30"),sQuery(id+"F12.wireOp",EDGE,"E31")])]});
            fillet(context, id + "F18", {"entities" : qUnion([Q0, Q1, Q2]), "radius" : 5 * mm, "tangentPropagation" : true, "allowEdgeOverflow" : false});
        }
    });
